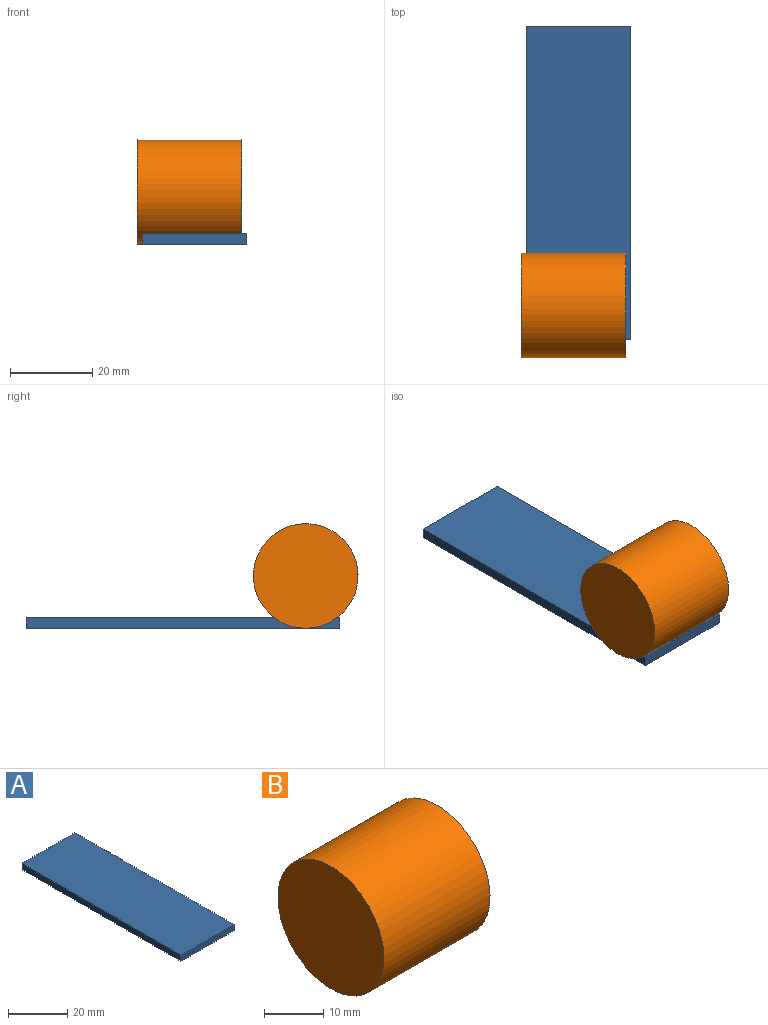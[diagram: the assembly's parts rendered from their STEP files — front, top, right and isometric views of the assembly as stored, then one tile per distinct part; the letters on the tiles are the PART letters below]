
ASSEMBLY  parts=2 mates=1
PART A: 6 faces, bbox 25.4x76.2x2.5 mm
  f0: plane 76.2x2.54mm, normal (1,0,0), area 193.5mm2, adj f1,f3,f4,f5
  f1: plane 25.4x2.54mm, normal (0,1,0), area 64.5mm2, adj f0,f2,f4,f5
  f2: plane 76.2x2.54mm, normal (-1,0,0), area 193.5mm2, adj f1,f3,f4,f5
  f3: plane 25.4x2.54mm, normal (0,-1,0), area 64.5mm2, adj f0,f2,f4,f5
  f4: plane 76.2x25.4mm, normal (0,0,1), area 1935.5mm2, adj f0,f1,f2,f3
  f5: plane 76.2x25.4mm, normal (0,0,-1), area 1935.5mm2, adj f0,f1,f2,f3
PART B: 3 faces, bbox 25.4x25.4x25.4 mm
  f0: cylinder r=12.7mm len=25.4mm, axis (-1,0,0), area 2026.8mm2, adj f1,f2
  f1: plane 25.4x25.4mm, normal (1,0,0), area 506.7mm2, adj f0
  f2: plane 25.4x25.4mm, normal (-1,0,0), area 506.7mm2, adj f0
PLACE A rot(axis=(1,0,0),180deg) t=(-2.07,-4.06,13.91)mm
PLACE B t=(-3.25,-33.9,8.83)mm
MATE parallel B.f0 <-> A.f2  axis (-1,0,0) through (-15.95,-33.9,24.07)mm
